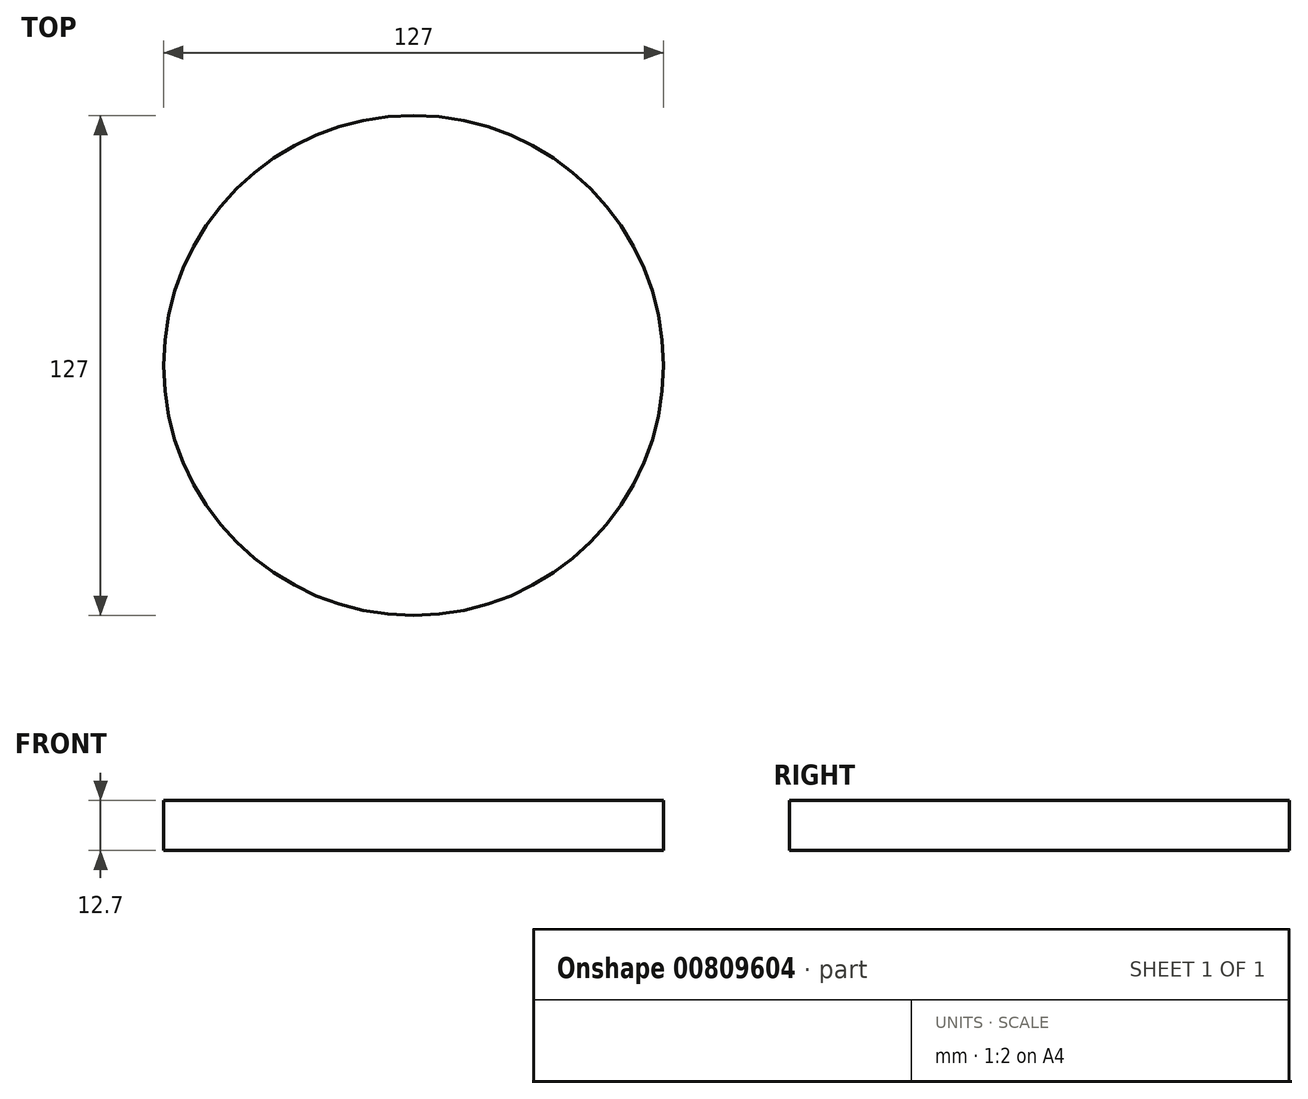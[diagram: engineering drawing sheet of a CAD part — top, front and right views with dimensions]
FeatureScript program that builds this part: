
annotation { "Feature Type Name" : "Feature", "Feature Type Description" : "" }
export const myFeature = defineFeature(function(context is Context, id is Id, definition is map)
    precondition{}
    {
        {
            var Q0;
            Q0=qCreatedBy(makeId("Top.planeOp"),FACE);
            var sketch = newSketch(context, id + "F0", { "sketchPlane" : qUnion([Q0])});
            skCircle(sketch, "E0", {"center": v(0, 0) * mm, "radius": 63.5 * mm});
            skSolve(sketch);
        }
        {
            var Q0;
            Q0 = qSketchRegion(id + "F0", true);
            extrude(context, id + "F1", {"entities" : qUnion([Q0]), "depth" : 12.7 * mm, "offsetDistance" : 25.4 * mm});
        }
    });
